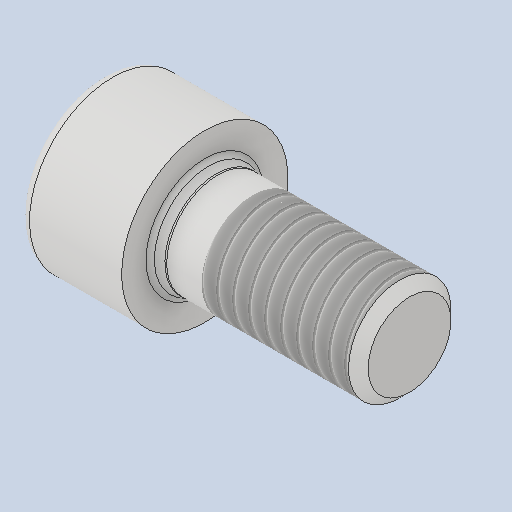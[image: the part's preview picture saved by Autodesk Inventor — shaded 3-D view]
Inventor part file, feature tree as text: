
AUTODESK INVENTOR PART (.ipt)
format: ipt  version: 2023 (Build 270158000, 158)  size: 230,400 bytes
history: native  units: mm
features: other x28, sketch x2, revolve x1, thread x1, extrude x1
ambient origin geometry x8: Origin, YZ Plane, XZ Plane, XY Plane, X Axis, Y Axis, Z Axis, Center Point
bodies: Solid1 (feature_tree)
feature tree (33):
  revolve  "Revolution1"  [1 undecoded]
  thread  "Thread1"  [1 undecoded]
  extrude  "Extrusion1"  [1 undecoded]
  other  "IP1_XY"
  other  "IP1_YZ"
  other  "IP1_ZX"
  other  "IP1_X"
  other  "IP1_Y"
  other  "IP1_Z"
  other  "IP1_Center"
  other  "IP2_XY"
  other  "IP2_YZ"
  other  "IP2_ZX"
  other  "IP2_X"
  other  "IP2_Y"
  other  "IP2_Z"
  other  "IP2_Center"
  other  "IP3_XY"
  other  "IP3_YZ"
  other  "IP3_ZX"
  other  "IP3_X"
  other  "IP3_Y"
  other  "IP3_Z"
  other  "IP3_Center"
  other  "P_GUS_1000_XY"
  other  "P_GUS_1000_YZ"
  other  "P_GUS_1000_ZX"
  other  "P_GUS_1000_X"
  other  "P_GUS_1000_Y"
  other  "P_GUS_1000_Z"
  other  "P_GUS_1000_Center"
  sketch  "Skizze_2"  dims[d5=0.0mm d6=0.0mm d7=0.0mm]
  sketch  "Skizze_1"  dims[d0=360.0deg d1=11.483mm d2=0.0mm d3=8.0mm d4=0.0mm]
note: 3 required parameter values undecoded (feature->parameter linkage not recoverable at this tier; creation-order binding heuristic only, values carry confidence <= 0.55)